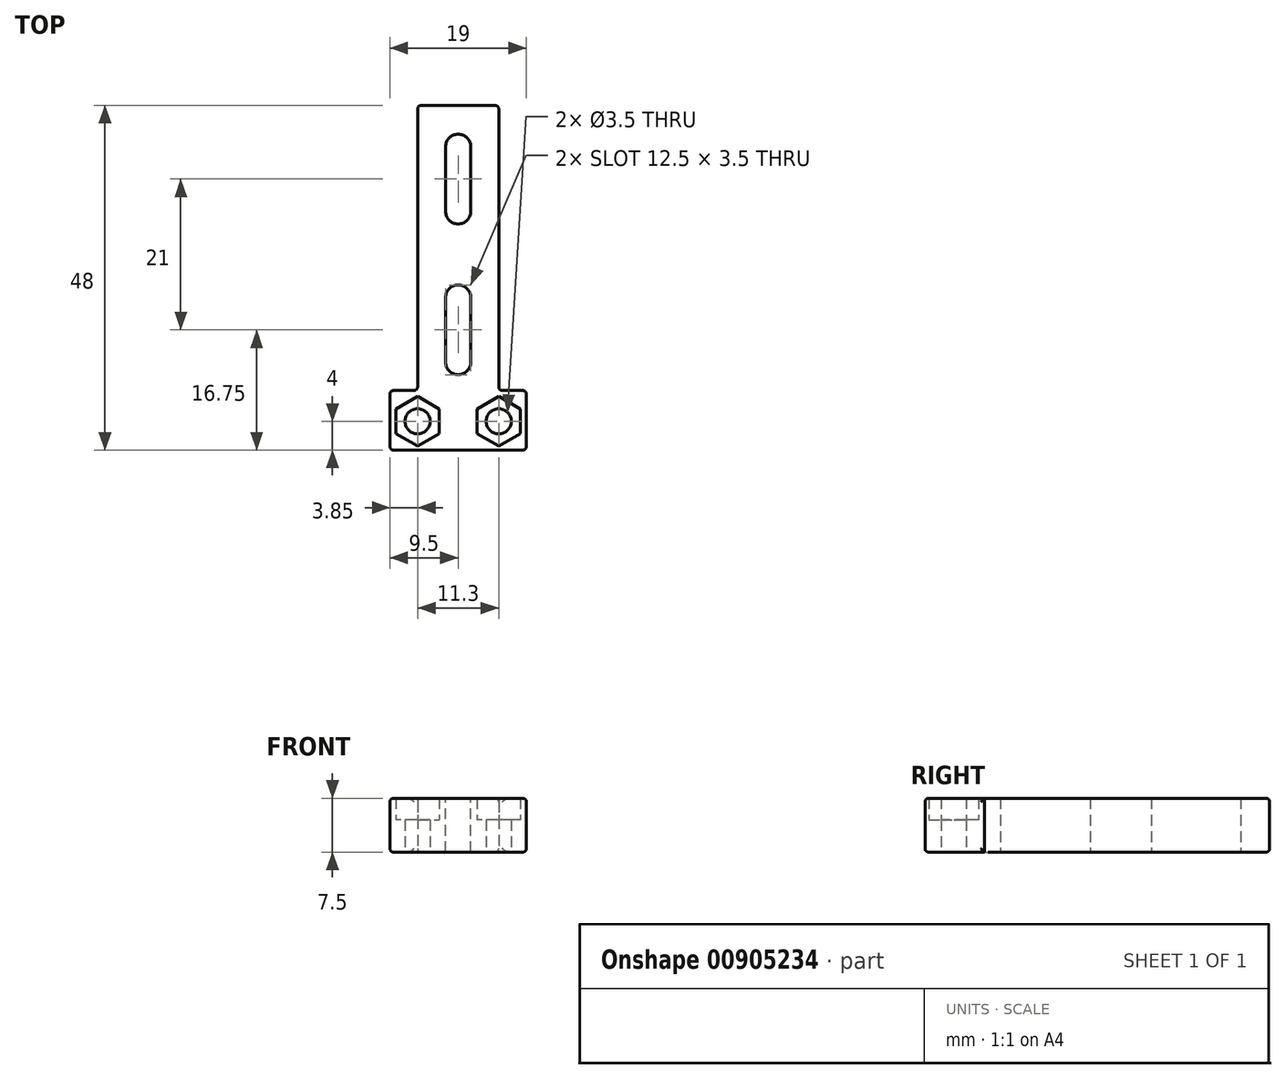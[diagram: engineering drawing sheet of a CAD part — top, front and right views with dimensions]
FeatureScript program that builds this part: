
annotation { "Feature Type Name" : "Feature", "Feature Type Description" : "" }
export const myFeature = defineFeature(function(context is Context, id is Id, definition is map)
    precondition{}
    {
        {
            var Q0;
            Q0=qCreatedBy(makeId("Top.planeOp"),FACE);
            var sketch = newSketch(context, id + "F0", { "sketchPlane" : qUnion([Q0])});
            skLineSegment(sketch, "E0.bottom", {"start": v(-5.65, 0) * mm, "end": v(5.65, 0) * mm});
            skLineSegment(sketch, "E0.top", {"start": v(-5.65, 48) * mm, "end": v(5.65, 48) * mm});
            skLineSegment(sketch, "E1.bottom", {"start": v(-9.5, 0) * mm, "end": v(9.5, 0) * mm});
            skLineSegment(sketch, "E1.left", {"start": v(-9.5, 0) * mm, "end": v(-9.5, 8.3) * mm});
            skCircle(sketch, "E2", {"center": v(-5.65, 4) * mm, "radius": 1.75 * mm});
            skCircle(sketch, "E3", {"center": v(5.65, 4) * mm, "radius": 1.75 * mm});
            skLineSegment(sketch, "E4", {"start": v(-9.5, 8.3) * mm, "end": v(-5.65, 8.3) * mm});
            skLineSegment(sketch, "E5", {"start": v(5.65, 11.46) * mm, "end": v(5.65, 48) * mm});
            skLineSegment(sketch, "E6", {"start": v(-5.65, 48) * mm, "end": v(-5.65, 8.3) * mm});
            skLineSegment(sketch, "E7", {"start": v(5.65, 11.46) * mm, "end": v(5.65, 10.55) * mm});
            skCircle(sketch, "E8", {"center": v(0, 42.25) * mm, "radius": 1.75 * mm});
            skCircle(sketch, "E9.MirrorC", {"center": v(0, 33.25) * mm, "radius": 1.75 * mm});
            skLineSegment(sketch, "E10", {"start": v(-1.78, 42.25) * mm, "end": v(-1.75, 33.24) * mm});
            skLineSegment(sketch, "E11", {"start": v(1.75, 33.26) * mm, "end": v(1.75, 42.25) * mm});
            skCircle(sketch, "E12.MirrorC", {"center": v(0, 21.25) * mm, "radius": 1.75 * mm});
            skCircle(sketch, "E13.MirrorC", {"center": v(0, 12.25) * mm, "radius": 1.75 * mm});
            skLineSegment(sketch, "E14.MirrorCS", {"start": v(1.75, 21.24) * mm, "end": v(1.75, 12.25) * mm});
            skLineSegment(sketch, "E15.MirrorCS", {"start": v(-1.78, 12.25) * mm, "end": v(-1.75, 21.26) * mm});
            skLineSegment(sketch, "E16", {"start": v(5.65, 10.55) * mm, "end": v(5.65, 8.3) * mm});
            skLineSegment(sketch, "E17", {"start": v(9.5, 8.3) * mm, "end": v(9.5, 0) * mm});
            skLineSegment(sketch, "E18", {"start": v(5.65, 8.3) * mm, "end": v(9.5, 8.3) * mm});
            skLineSegment(sketch, "E19.0", {"start": v(-2.65, 5.73) * mm, "end": v(-2.65, 2.27) * mm});
            skLineSegment(sketch, "E19.1", {"start": v(-2.65, 2.27) * mm, "end": v(-5.65, 0.54) * mm});
            skLineSegment(sketch, "E19.2", {"start": v(-5.65, 0.54) * mm, "end": v(-8.65, 2.27) * mm});
            skLineSegment(sketch, "E19.3", {"start": v(-8.65, 2.27) * mm, "end": v(-8.65, 5.73) * mm});
            skLineSegment(sketch, "E19.4", {"start": v(-8.65, 5.73) * mm, "end": v(-5.65, 7.46) * mm});
            skLineSegment(sketch, "E19.5", {"start": v(-5.65, 7.46) * mm, "end": v(-2.65, 5.73) * mm});
            skPoint(sketch, "E19.0.midPoint", {"position": v(-2.65, 4) * mm});
            skLineSegment(sketch, "E20.MirrorCS", {"start": v(5.65, 7.46) * mm, "end": v(2.65, 5.73) * mm});
            skLineSegment(sketch, "E21.MirrorCS", {"start": v(8.65, 5.73) * mm, "end": v(5.65, 7.46) * mm});
            skLineSegment(sketch, "E22.MirrorCS", {"start": v(8.65, 2.27) * mm, "end": v(8.65, 5.73) * mm});
            skLineSegment(sketch, "E23.MirrorCS", {"start": v(5.65, 0.54) * mm, "end": v(8.65, 2.27) * mm});
            skLineSegment(sketch, "E24.MirrorCS", {"start": v(2.65, 2.27) * mm, "end": v(5.65, 0.54) * mm});
            skLineSegment(sketch, "E25.MirrorCS", {"start": v(2.65, 5.73) * mm, "end": v(2.65, 2.27) * mm});
            skSolve(sketch);
        }
        {
            var Q0;
            Q0=makeQuery(id+"F0.imprint","IMPRINT",FACE,{"disambiguationData":[TD([[makeQuery(id+"F0.imprint","IMPRINT",EDGE,{"derivedFrom":sQuery(id+"F0.wireOp",EDGE,"E0.top")}),-1.0]])]});
            extrude(context, id + "F1", {"entities" : qUnion([Q0]), "depth" : 7.5 * mm, "offsetDistance" : 25 * mm});
        }
        {
            var Q0;
            Q0=makeQuery(id+"F0.imprint","IMPRINT",FACE,{"disambiguationData":[TD([[makeQuery(id+"F0.imprint","IMPRINT",EDGE,{"derivedFrom":sQuery(id+"F0.wireOp",EDGE,"E2")}),-1.0]])]});
            extrude(context, id + "F2", {"entities" : qUnion([Q0]), "operationType" : NewBodyOperationType.ADD, "depth" : 4.5 * mm, "offsetDistance" : 25 * mm});
        }
        {
            var Q0;
            Q0=makeQuery(id+"F0.imprint","IMPRINT",FACE,{"disambiguationData":[TD([[makeQuery(id+"F0.imprint","IMPRINT",EDGE,{"derivedFrom":sQuery(id+"F0.wireOp",EDGE,"E3")}),-1.0]])]});
            extrude(context, id + "F3", {"entities" : qUnion([Q0]), "operationType" : NewBodyOperationType.ADD, "depth" : 4.5 * mm, "offsetDistance" : 25 * mm});
        }
        {
            var Q0;
            Q0=makeQuery(id+"F1.opExtrude","CAP_FACE",FACE,{"disambiguationData":[OSD([sQuery(id+"F0.wireOp",EDGE,"E0.top"),sQuery(id+"F0.wireOp",EDGE,"E1.bottom"),sQuery(id+"F0.wireOp",EDGE,"E1.left"),sQuery(id+"F0.wireOp",EDGE,"E4"),sQuery(id+"F0.wireOp",EDGE,"E5"),sQuery(id+"F0.wireOp",EDGE,"E6"),sQuery(id+"F0.wireOp",EDGE,"E7"),sQuery(id+"F0.wireOp",EDGE,"E8"),sQuery(id+"F0.wireOp",EDGE,"E9.MirrorC"),sQuery(id+"F0.wireOp",EDGE,"E12.MirrorC"),sQuery(id+"F0.wireOp",EDGE,"E13.MirrorC"),sQuery(id+"F0.wireOp",EDGE,"E16"),sQuery(id+"F0.wireOp",EDGE,"E17"),sQuery(id+"F0.wireOp",EDGE,"E18"),sQuery(id+"F0.wireOp",EDGE,"E19.0"),sQuery(id+"F0.wireOp",EDGE,"E19.1"),sQuery(id+"F0.wireOp",EDGE,"E19.2"),sQuery(id+"F0.wireOp",EDGE,"E19.3"),sQuery(id+"F0.wireOp",EDGE,"E19.4"),sQuery(id+"F0.wireOp",EDGE,"E19.5"),sQuery(id+"F0.wireOp",EDGE,"E20.MirrorCS"),sQuery(id+"F0.wireOp",EDGE,"E21.MirrorCS"),sQuery(id+"F0.wireOp",EDGE,"E22.MirrorCS"),sQuery(id+"F0.wireOp",EDGE,"E23.MirrorCS"),sQuery(id+"F0.wireOp",EDGE,"E24.MirrorCS"),sQuery(id+"F0.wireOp",EDGE,"E25.MirrorCS")])],"isStart":false});
            var sketch = newSketch(context, id + "F4", { "sketchPlane" : qUnion([Q0])});
            skLineSegment(sketch, "E26", {"start": v(-1.75, 12.25) * mm, "end": v(-1.75, 21.4) * mm});
            skLineSegment(sketch, "E27", {"start": v(1.75, 21.25) * mm, "end": v(1.75, 12.25) * mm});
            skLineSegment(sketch, "E28", {"start": v(-1.75, 33.25) * mm, "end": v(-1.75, 42.25) * mm});
            skLineSegment(sketch, "E29", {"start": v(1.75, 42.25) * mm, "end": v(1.75, 33.25) * mm});
            skSolve(sketch);
        }
        {
            var Q0;
            {var subQ5=sQuery(id+"F4.wireOp",EDGE,"E27");Q0=makeQuery(id+"F4.imprint","IMPRINT",FACE,{"disambiguationData":[TD([[makeQuery(id+"F4.imprint","IMPRINT",EDGE,{"derivedFrom":subQ5}),-1.0]])]});}
            extrude(context, id + "F5", {"entities" : qUnion([Q0]), "operationType" : NewBodyOperationType.REMOVE, "oppositeDirection" : true, "depth" : 8.8 * mm, "offsetDistance" : 25 * mm});
        }
        {
            var Q0;
            Q0=makeQuery(id+"F1.opExtrude","CAP_FACE",FACE,{"disambiguationData":[OSD([sQuery(id+"F0.wireOp",EDGE,"E0.top"),sQuery(id+"F0.wireOp",EDGE,"E1.bottom"),sQuery(id+"F0.wireOp",EDGE,"E1.left"),sQuery(id+"F0.wireOp",EDGE,"E4"),sQuery(id+"F0.wireOp",EDGE,"E5"),sQuery(id+"F0.wireOp",EDGE,"E6"),sQuery(id+"F0.wireOp",EDGE,"E7"),sQuery(id+"F0.wireOp",EDGE,"E8"),sQuery(id+"F0.wireOp",EDGE,"E9.MirrorC"),sQuery(id+"F0.wireOp",EDGE,"E12.MirrorC"),sQuery(id+"F0.wireOp",EDGE,"E13.MirrorC"),sQuery(id+"F0.wireOp",EDGE,"E16"),sQuery(id+"F0.wireOp",EDGE,"E17"),sQuery(id+"F0.wireOp",EDGE,"E18"),sQuery(id+"F0.wireOp",EDGE,"E19.0"),sQuery(id+"F0.wireOp",EDGE,"E19.1"),sQuery(id+"F0.wireOp",EDGE,"E19.2"),sQuery(id+"F0.wireOp",EDGE,"E19.3"),sQuery(id+"F0.wireOp",EDGE,"E19.4"),sQuery(id+"F0.wireOp",EDGE,"E19.5"),sQuery(id+"F0.wireOp",EDGE,"E20.MirrorCS"),sQuery(id+"F0.wireOp",EDGE,"E21.MirrorCS"),sQuery(id+"F0.wireOp",EDGE,"E22.MirrorCS"),sQuery(id+"F0.wireOp",EDGE,"E23.MirrorCS"),sQuery(id+"F0.wireOp",EDGE,"E24.MirrorCS"),sQuery(id+"F0.wireOp",EDGE,"E25.MirrorCS")])],"isStart":false});
            var sketch = newSketch(context, id + "F6", { "sketchPlane" : qUnion([Q0])});
            skLineSegment(sketch, "E30", {"start": v(-1.75, 33.25) * mm, "end": v(-1.75, 42.25) * mm});
            skLineSegment(sketch, "E31", {"start": v(1.75, 42.25) * mm, "end": v(1.75, 33.25) * mm});
            skSolve(sketch);
        }
        {
            var Q0;
            {var subQ0=sQuery(id+"F6.wireOp",EDGE,"E30");Q0=makeQuery(id+"F6.imprint","IMPRINT",FACE,{"disambiguationData":[TD([[makeQuery(id+"F6.imprint","IMPRINT",EDGE,{"derivedFrom":subQ0}),-1.0]])]});}
            extrude(context, id + "F7", {"entities" : qUnion([Q0]), "operationType" : NewBodyOperationType.REMOVE, "oppositeDirection" : true, "depth" : 25 * mm, "offsetDistance" : 25 * mm});
        }
        {
            var Q0;
            Q0=makeQuery(id+"F1.opExtrude","SWEPT_EDGE",EDGE,{"disambiguationData":[OSD([sQuery(id+"F0.wireOp",EDGE,"E0.top"),sQuery(id+"F0.wireOp",EDGE,"E6")])]});
            var Q1;
            Q1=makeQuery(id+"F1.opExtrude","SWEPT_EDGE",EDGE,{"disambiguationData":[OSD([sQuery(id+"F0.wireOp",EDGE,"E0.top"),sQuery(id+"F0.wireOp",EDGE,"E5")])]});
            var Q2;
            Q2=makeQuery(id+"F1.opExtrude","SWEPT_EDGE",EDGE,{"disambiguationData":[OSD([sQuery(id+"F0.wireOp",EDGE,"E17"),sQuery(id+"F0.wireOp",EDGE,"E18")])]});
            var Q3;
            Q3=makeQuery(id+"F1.opExtrude","SWEPT_EDGE",EDGE,{"disambiguationData":[OSD([sQuery(id+"F0.wireOp",EDGE,"E1.left"),sQuery(id+"F0.wireOp",EDGE,"E4")])]});
            var Q4;
            Q4=makeQuery(id+"F1.opExtrude","SWEPT_EDGE",EDGE,{"disambiguationData":[OSD([sQuery(id+"F0.wireOp",EDGE,"E1.bottom"),sQuery(id+"F0.wireOp",EDGE,"E1.left")])]});
            var Q5;
            Q5=makeQuery(id+"F1.opExtrude","SWEPT_FACE",FACE,{"disambiguationData":[OSD([sQuery(id+"F0.wireOp",EDGE,"E17")])]});
            var Q6;
            Q6=makeQuery(id+"F1.opExtrude","SWEPT_FACE",FACE,{"disambiguationData":[OSD([sQuery(id+"F0.wireOp",EDGE,"E5"),sQuery(id+"F0.wireOp",EDGE,"E7"),sQuery(id+"F0.wireOp",EDGE,"E16")])]});
            var Q7;
            Q7=makeQuery(id+"F1.opExtrude","SWEPT_FACE",FACE,{"disambiguationData":[OSD([sQuery(id+"F0.wireOp",EDGE,"E6")])]});
            var Q8;
            Q8=makeQuery(id+"F1.opExtrude","SWEPT_FACE",FACE,{"disambiguationData":[OSD([sQuery(id+"F0.wireOp",EDGE,"E1.left")])]});
            var Q9;
            Q9=makeQuery(id+"F1.opExtrude","SWEPT_FACE",FACE,{"disambiguationData":[OSD([sQuery(id+"F0.wireOp",EDGE,"E0.top")])]});
            var Q10;
            Q10=makeQuery(id+"F1.opExtrude","SWEPT_FACE",FACE,{"disambiguationData":[OSD([sQuery(id+"F0.wireOp",EDGE,"E1.bottom")])]});
            fillet(context, id + "F8", {"entities" : qUnion([Q0, Q1, Q2, Q3, Q4, Q5, Q6, Q7, Q8, Q9, Q10]), "radius" : 0.5 * mm, "tangentPropagation" : true, "allowEdgeOverflow" : false});
        }
    });
